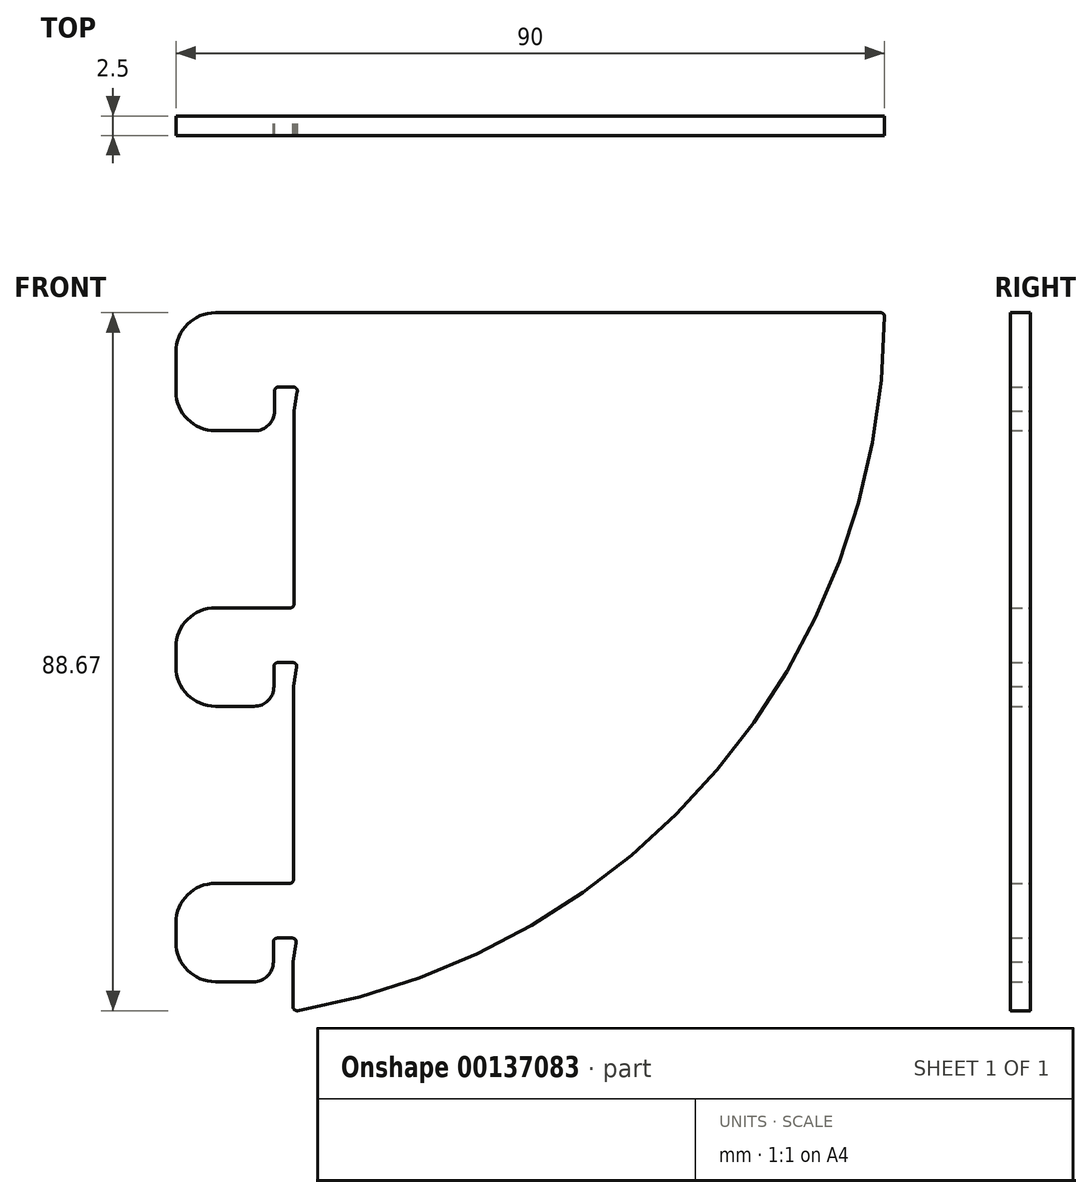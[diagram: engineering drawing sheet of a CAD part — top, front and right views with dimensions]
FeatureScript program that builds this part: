
annotation { "Feature Type Name" : "Feature", "Feature Type Description" : "" }
export const myFeature = defineFeature(function(context is Context, id is Id, definition is map)
    precondition{}
    {
        {
            var Q0;
            Q0=qCreatedBy(makeId("Front.planeOp"),FACE);
            var sketch = newSketch(context, id + "F0", { "sketchPlane" : qUnion([Q0])});
            skLineSegment(sketch, "E0", {"start": v(0, -5) * mm, "end": v(0, -15) * mm});
            skLineSegment(sketch, "E1", {"start": v(89.5, 0) * mm, "end": v(5, 0) * mm});
            skArc(sketch, "E2", {"start": v(15.44, -88.66) * mm, "mid": v(68.72, -58.11) * mm, "end": v(90, -0.5) * mm});
            skArc(sketch, "E3.filletArc", {"start": v(5, 0) * mm, "mid": v(1.46, -1.46) * mm, "end": v(0, -5) * mm});
            skLineSegment(sketch, "E4", {"start": v(0, 0) * mm, "end": v(0, -15) * mm});
            skLineSegment(sketch, "E5", {"start": v(0, -15) * mm, "end": v(10, -15) * mm});
            skLineSegment(sketch, "E6", {"start": v(12.5, -12.5) * mm, "end": v(12.5, -9.95) * mm});
            skLineSegment(sketch, "E7", {"start": v(14.5, -37.5) * mm, "end": v(0, -37.5) * mm});
            skLineSegment(sketch, "E8", {"start": v(15, -37) * mm, "end": v(15, -12.5) * mm});
            skLineSegment(sketch, "E9", {"start": v(15, -12.5) * mm, "end": v(15.4, -10.03) * mm});
            skLineSegment(sketch, "E10", {"start": v(14.91, -9.45) * mm, "end": v(13, -9.45) * mm});
            skLineSegment(sketch, "E11.trimOffspring", {"start": v(0, -37.5) * mm, "end": v(0, -50) * mm});
            skLineSegment(sketch, "E12.1.0.0", {"start": v(-0.07, -50) * mm, "end": v(9.93, -50) * mm});
            skLineSegment(sketch, "E12.1.0.1", {"start": v(12.43, -47.5) * mm, "end": v(12.43, -44.95) * mm});
            skLineSegment(sketch, "E12.1.0.2", {"start": v(14.84, -44.45) * mm, "end": v(12.93, -44.45) * mm});
            skLineSegment(sketch, "E12.1.0.3", {"start": v(14.93, -47.5) * mm, "end": v(15.33, -45.03) * mm});
            skLineSegment(sketch, "E12.1.0.4", {"start": v(14.93, -72) * mm, "end": v(14.93, -47.5) * mm});
            skLineSegment(sketch, "E12.1.0.5", {"start": v(14.43, -72.5) * mm, "end": v(-0.07, -72.5) * mm});
            skLineSegment(sketch, "E12.2.0.0", {"start": v(-0.14, -85) * mm, "end": v(9.86, -85) * mm});
            skLineSegment(sketch, "E12.2.0.1", {"start": v(12.36, -82.5) * mm, "end": v(12.36, -79.95) * mm});
            skLineSegment(sketch, "E12.2.0.2", {"start": v(14.77, -79.45) * mm, "end": v(12.86, -79.45) * mm});
            skLineSegment(sketch, "E12.2.0.3", {"start": v(14.86, -82.5) * mm, "end": v(15.26, -80.03) * mm});
            skLineSegment(sketch, "E12.2.0.4", {"start": v(14.86, -88.17) * mm, "end": v(14.86, -82.5) * mm});
            skLineSegment(sketch, "E12.direction1", {"start": v(0, -37.5) * mm, "end": v(-0.03, -50) * mm, "construction": true});
            skLineSegment(sketch, "E13.trimOffspring", {"start": v(0, -72.5) * mm, "end": v(0, -85) * mm});
            skPoint(sketch, "E14.orphan", {"position": v(0, -90) * mm});
            skPoint(sketch, "E15.visualSharp", {"position": v(12.36, -85) * mm});
            skArc(sketch, "E15.filletArc", {"start": v(9.86, -85) * mm, "mid": v(11.63, -84.27) * mm, "end": v(12.36, -82.5) * mm});
            skPoint(sketch, "E16.visualSharp", {"position": v(12.43, -50) * mm});
            skArc(sketch, "E16.filletArc", {"start": v(9.93, -50) * mm, "mid": v(11.7, -49.27) * mm, "end": v(12.43, -47.5) * mm});
            skPoint(sketch, "E17.visualSharp", {"position": v(12.5, -15) * mm});
            skArc(sketch, "E17.filletArc", {"start": v(10, -15) * mm, "mid": v(11.77, -14.27) * mm, "end": v(12.5, -12.5) * mm});
            skPoint(sketch, "E18.visualSharp", {"position": v(15.5, -9.45) * mm});
            skArc(sketch, "E18.filletArc", {"start": v(15.4, -10.03) * mm, "mid": v(15.3, -9.63) * mm, "end": v(14.91, -9.45) * mm});
            skPoint(sketch, "E19.visualSharp", {"position": v(12.5, -9.45) * mm});
            skArc(sketch, "E19.filletArc", {"start": v(13, -9.45) * mm, "mid": v(12.65, -9.6) * mm, "end": v(12.5, -9.95) * mm});
            skPoint(sketch, "E20.visualSharp", {"position": v(15, -37.5) * mm});
            skArc(sketch, "E20.filletArc", {"start": v(14.5, -37.5) * mm, "mid": v(14.85, -37.35) * mm, "end": v(15, -37) * mm});
            skPoint(sketch, "E21.visualSharp", {"position": v(12.43, -44.45) * mm});
            skArc(sketch, "E21.filletArc", {"start": v(12.93, -44.45) * mm, "mid": v(12.58, -44.6) * mm, "end": v(12.43, -44.95) * mm});
            skPoint(sketch, "E22.visualSharp", {"position": v(15.43, -44.45) * mm});
            skArc(sketch, "E22.filletArc", {"start": v(15.33, -45.03) * mm, "mid": v(15.22, -44.63) * mm, "end": v(14.84, -44.45) * mm});
            skPoint(sketch, "E23.visualSharp", {"position": v(12.36, -79.45) * mm});
            skArc(sketch, "E23.filletArc", {"start": v(12.86, -79.45) * mm, "mid": v(12.5, -79.6) * mm, "end": v(12.36, -79.95) * mm});
            skPoint(sketch, "E24.visualSharp", {"position": v(15.36, -79.45) * mm});
            skArc(sketch, "E24.filletArc", {"start": v(15.26, -80.03) * mm, "mid": v(15.15, -79.63) * mm, "end": v(14.77, -79.45) * mm});
            skPoint(sketch, "E25.visualSharp", {"position": v(14.93, -72.5) * mm});
            skArc(sketch, "E25.filletArc", {"start": v(14.43, -72.5) * mm, "mid": v(14.78, -72.35) * mm, "end": v(14.93, -72) * mm});
            skPoint(sketch, "E26.visualSharp", {"position": v(14.86, -88.76) * mm});
            skArc(sketch, "E26.filletArc", {"start": v(14.86, -88.17) * mm, "mid": v(15.04, -88.55) * mm, "end": v(15.44, -88.66) * mm});
            skPoint(sketch, "E27.visualSharp", {"position": v(90, 0) * mm});
            skArc(sketch, "E27.filletArc", {"start": v(90, -0.5) * mm, "mid": v(89.85, -0.15) * mm, "end": v(89.5, 0) * mm});
            skSolve(sketch);
        }
        {
            var Q0;
            Q0 = qSketchRegion(id + "F0", true);
            extrude(context, id + "F1", {"entities" : qUnion([Q0]), "depth" : 2.5 * mm});
        }
        {
            var Q0;
            Q0=makeQuery(id+"F1.opExtrude","SWEPT_EDGE",EDGE,{"disambiguationData":[OSD([sQuery(id+"F0.wireOp",EDGE,"E4"),sQuery(id+"F0.wireOp",EDGE,"E5")])]});
            var Q1;
            Q1=makeQuery(id+"F1.opExtrude","SWEPT_EDGE",EDGE,{"disambiguationData":[OSD([sQuery(id+"F0.wireOp",EDGE,"E11.trimOffspring"),sQuery(id+"F0.wireOp",EDGE,"E12.1.0.0")])]});
            var Q2;
            Q2=makeQuery(id+"F1.opExtrude","SWEPT_EDGE",EDGE,{"disambiguationData":[OSD([sQuery(id+"F0.wireOp",EDGE,"E7"),sQuery(id+"F0.wireOp",EDGE,"E11.trimOffspring")])]});
            var Q3;
            Q3=makeQuery(id+"F1.opExtrude","SWEPT_EDGE",EDGE,{"disambiguationData":[OSD([sQuery(id+"F0.wireOp",EDGE,"E12.2.0.0"),sQuery(id+"F0.wireOp",EDGE,"E13.trimOffspring")])]});
            var Q4;
            Q4=makeQuery(id+"F1.opExtrude","SWEPT_EDGE",EDGE,{"disambiguationData":[OSD([sQuery(id+"F0.wireOp",EDGE,"E12.1.0.5"),sQuery(id+"F0.wireOp",EDGE,"E13.trimOffspring")])]});
            fillet(context, id + "F2", {"entities" : qUnion([Q0, Q1, Q2, Q3, Q4]), "radius" : 5 * mm, "tangentPropagation" : true, "allowEdgeOverflow" : false});
        }
    });
